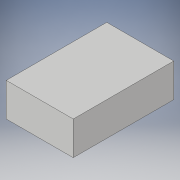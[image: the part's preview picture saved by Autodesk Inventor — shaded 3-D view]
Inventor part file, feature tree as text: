
AUTODESK INVENTOR PART (.ipt)
format: ipt  version: 2019.4 (Build 234330000, 330)  size: 86,528 bytes
history: native  units: in
note: dims shown in document units (in); Inventor stores cm internally (conversion verified against a paired STEP export)
features: extrude x1, sketch x1
ambient origin geometry x8: Origin, YZ Plane, XZ Plane, XY Plane, X Axis, Y Axis, Z Axis, Center Point
bodies: Solid1 (feature_tree)
feature tree (2):
  extrude  "Extrusion1"  Depth=1.1811in
  sketch  "Sketch1"  dims[d0=0.7874in d1=1.1811in d2=0.3937in d3=0.0in]
